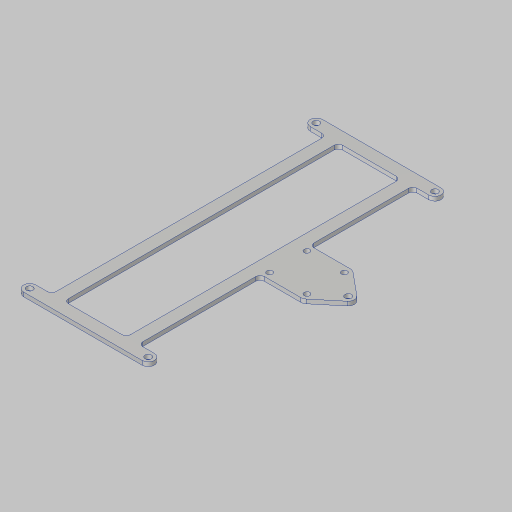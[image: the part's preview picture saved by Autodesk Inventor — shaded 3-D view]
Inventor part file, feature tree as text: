
AUTODESK INVENTOR PART (.ipt)
format: ipt  version: 2023.5 (Build 275446000, 446)  size: 232,960 bytes
history: native  units: in
note: dims shown in document units (in); Inventor stores cm internally (conversion verified against a paired STEP export)
features: sketch x4, extrude x3, hole x3, projected_geometry x3, fillet x2
ambient origin geometry x8: Origin, YZ Plane, XZ Plane, XY Plane, X Axis, Y Axis, Z Axis, Center Point
bodies: Solid1 (feature_tree)
feature tree (15):
  sketch  "Sketch1"  dims[d0=0.375in d1=3.62in]
  extrude  "Extrusion1"  Depth=0.375in
  sketch  "Sketch2"  dims[d2=8.75in d4=0.375in]
  hole  "Hole1"  [1 undecoded]
  sketch  "Sketch3"  dims[d5=1.9in d6=0.375in d7=0.375in]
  extrude  "Extrusion2"  Depth=0.375in
  fillet  "Fillet2"  Radius=0.375in
  hole  "Hole4"  [1 undecoded]
  sketch  "Sketch5"  dims[d16=0.125in d17=0.0in d18=0.201in d19=0.75in d20=0.385in d21=0.25in d22=0.5635in d23=1.0in d24=0.8108in d33=1.14in d34=1.14in d35=0.375in d36=0.375in d37=0.625in d38=0.625in d39=0.625in d40=0.625in d48=1.245in d50=1.14in d51=0.375in d55=0.125in d56=0.0in d57=0.13in d58=0.177in d59=0.276in d60=0.332in d61=0.25in d62=0.5635in d63=1.0in d64=0.8108in d66=0.28in d67=1.14in d76=0.375in d77=0.5in d78=1.0in d79=0.0in d80=0.201in d81=0.432in d82=0.385in d83=0.25in d84=0.5635in d85=1.0in d86=0.8108in d87=0.125in]
  extrude  "Extrusion3"  Depth=0.125in
  hole  "Hole6"  [1 undecoded]
  fillet  "Fillet3"  Radius=0.375in
  projected_geometry  "Projected Loop1"
  projected_geometry  "Project Cut Edges1"
  projected_geometry  "Project Cut Edges2"
note: 3 required parameter values undecoded (feature->parameter linkage not recoverable at this tier; creation-order binding heuristic only, values carry confidence <= 0.55)
